# Revit family: Siella_G5 600x600
name_source: partatom
category: Lighting Fixtures
revit_build: Autodesk Revit 2018 (Build: 20190510_1515(x64)
units: mm (PartAtom-declared; Revit-internal decimal feet)

## family parameters
Cut with Voids When Loaded = No
Host = Face
Light Source = No
OmniClass Number = 23.80.70.14
OmniClass Title = Luminaries for External Lighting
Part Type = Normal
Room Calculation Point = No
Round Connector Dimension = Use Diameter
Shared = Yes

## types (16) — shared parameters
Apparent Load = 33 VA
CRI = 80
Color = RAL9016 Verkehrsweiß
Connection Load = 33 VA
Degree of protection = IP40
LS_offset = 1 mm  [stored 0.00328084 ft]
Lamp = LED
Lamp_0 = LED
Manufacturer = TRILUX
Mat = TRILUX_RAL9016
Safety class = I
URL = http://www.trilux.com
h = 13 mm
l = 595 mm  [stored 1.9521 ft]
l_offset = 547 mm
w = 595 mm  [stored 1.9521 ft]
w_offset = 547 mm
zero-valued in all types: Default Elevation

## per-type parameters (varying)
| type | CENFluxCode | Colour temperature (K) | Dimming/Balast | Light Source | Luminous flux of luminaire (lm) | SEO | TK | TOC | Weight |
| Siella G5 M73 OTA22 LED3600-840 ETDD TWW | 47 78 95 100 100 0 0 0 0 | 4000 | ETDD | Siella_G5_LS : TX060605 | 3600 | TRILUX_WH_4000 | 10175378 | 7164551 | 2.2 |
| Siella G5 M73 OTA22 LED3600-840 ET TWW | 47 78 95 100 100 0 0 0 0 | 4000 | ET | Siella_G5_LS : TX060605 | 3600 | TRILUX_WH_4000 | 10175377 | 7164540 | 2.2 |
| Siella G5 M73 OTA22 LED3600-840 ETDD | 47 78 95 100 100 0 0 0 0 | 4000 | ETDD | Siella_G5_LS : TX060604 | 3600 | TRILUX_WH_4000 | 10175376 | 7164451 | 2 |
| Siella G5 M73 OTA22 LED3600-840 ET | 47 78 95 100 100 0 0 0 0 | 4000 | ET | Siella_G5_LS : TX060604 | 3600 | TRILUX_WH_4000 | 10175375 | 7164440 | 2 |
| Siella G5 M73 OTA22 LED3400-830 ETDD TWW | 47 78 95 100 100 0 0 0 0 | 3000 | ETDD | Siella_G5_LS : TX060603 | 3400 | TRILUX_WH_3000 | 10175374 | 7164351 | 2.2 |
| Siella G5 M73 OTA22 LED3400-830 ET TWW | 47 78 95 100 100 0 0 0 0 | 3000 | ET | Siella_G5_LS : TX060603 | 3400 | TRILUX_WH_3000 | 10175373 | 7164340 | 2.2 |
| Siella G5 M73 OTA22 LED3400-830 ETDD | 47 78 95 100 100 0 0 0 0 | 3000 | ETDD | Siella_G5_LS : TX060602 | 3400 | TRILUX_WH_3000 | 10175372 | 7164251 | 2 |
| Siella G5 M73 OTA22 LED3400-830 ET | 47 78 95 100 100 0 0 0 0 | 3000 | ET | Siella_G5_LS : TX060602 | 3400 | TRILUX_WH_3000 | 10175371 | 7164240 | 2 |
| Siella G5 M73 OTA19 LED3600-840 ETDD TWW | 58 85 97 100 100 0 0 0 0 | 4000 | ETDD | Siella_G5_LS : TX060601 | 3600 | TRILUX_WH_4000 | 10175390 | 7165151 | 2.2 |
| Siella G5 M73 OTA19 LED3600-840 ET TWW | 58 85 97 100 100 0 0 0 0 | 4000 | ET | Siella_G5_LS : TX060601 | 3600 | TRILUX_WH_4000 | 10175388 | 7165140 | 2.2 |
| Siella G5 M73 OTA19 LED3600-840 ETDD | 58 85 97 100 100 0 0 0 0 | 4000 | ETDD | Siella_G5_LS : TX060600 | 3600 | TRILUX_WH_4000 | 10175389 | 7165051 | 2 |
| Siella G5 M73 OTA19 LED3600-840 ET | 58 85 97 100 100 0 0 0 0 | 4000 | ET | Siella_G5_LS : TX060600 | 3600 | TRILUX_WH_4000 | 10175387 | 7165040 | 2 |
| Siella G5 M73 OTA19 LED3400-830 ETDD TWW | 58 85 97 100 100 0 0 0 0 | 3000 | ETDD | Siella_G5_LS : TX060599 | 3400 | TRILUX_WH_3000 | 10175386 | 7164951 | 2.2 |
| Siella G5 M73 OTA19 LED3400-830 ET TWW | 58 85 97 100 100 0 0 0 0 | 3000 | ET | Siella_G5_LS : TX060599 | 3400 | TRILUX_WH_3000 | 10175384 | 7164940 | 2 |
| Siella G5 M73 OTA19 LED3400-830 ETDD | 58 85 97 100 100 0 0 0 0 | 3000 | ETDD | Siella_G5_LS : TX060598 | 3400 | TRILUX_WH_3000 | 10175385 | 7164851 | 2 |
| Siella G5 M73 OTA19 LED3400-830 ET | 58 85 97 100 100 0 0 0 0 | 3000 | ET | Siella_G5_LS : TX060598 | 3400 | TRILUX_WH_3000 | 10175383 | 7164840 | 2 |

note: [stored X ft] marks values corroborated as IEEE doubles in the binary element streams (Revit-internal decimal feet)

## geometry (parser evidence)
native form markers: Sweep x5
no freeform markers — native parametric forms only
